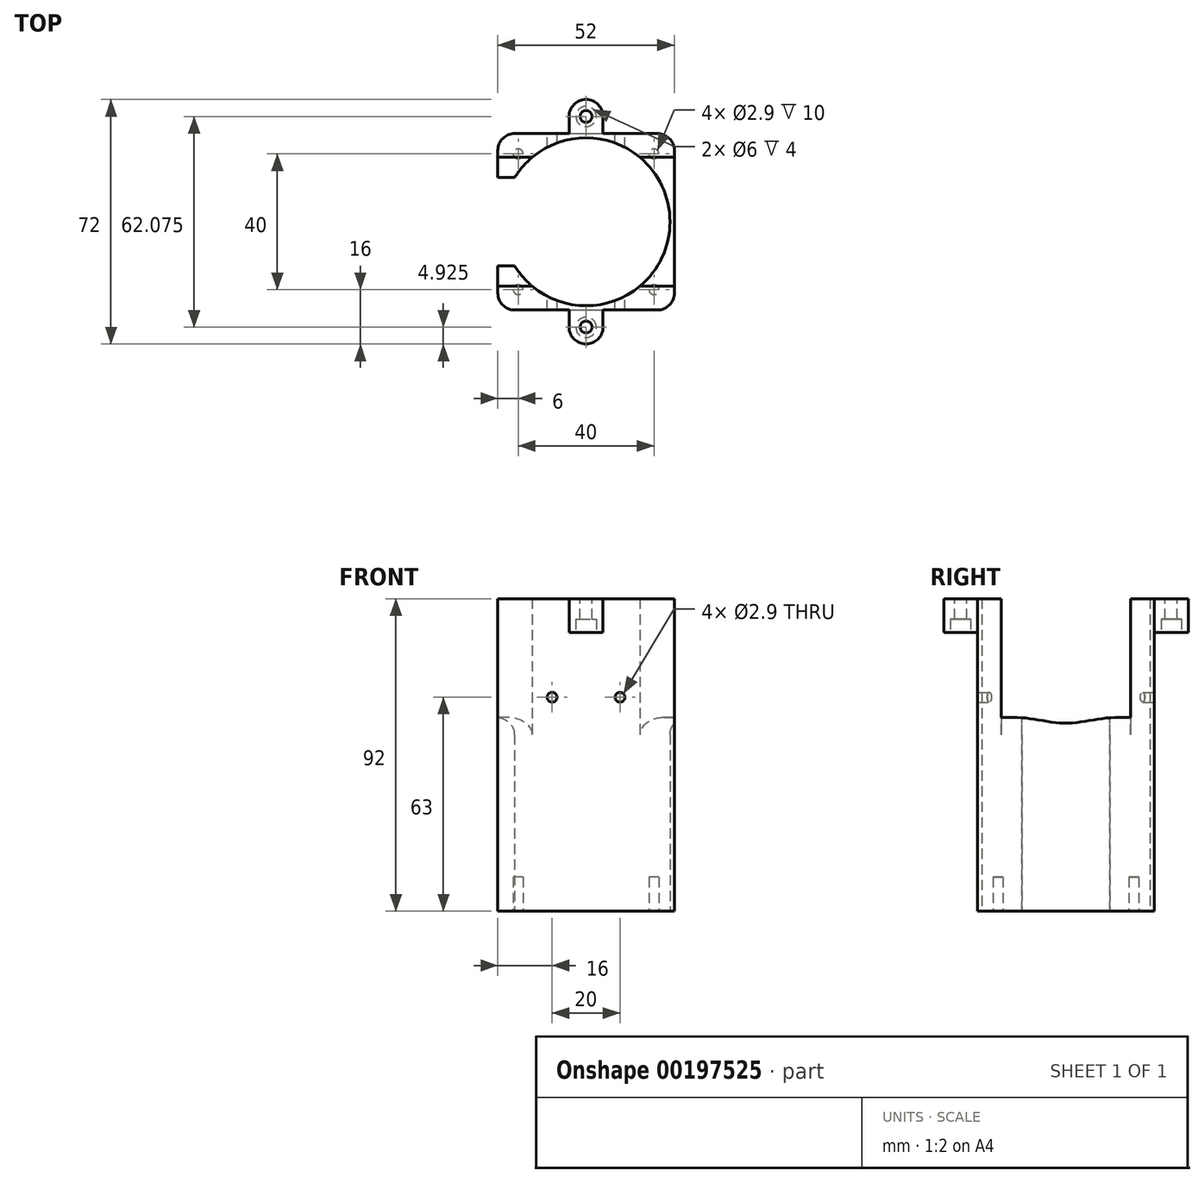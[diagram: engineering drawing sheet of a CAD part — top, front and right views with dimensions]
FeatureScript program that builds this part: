
annotation { "Feature Type Name" : "Feature", "Feature Type Description" : "" }
export const myFeature = defineFeature(function(context is Context, id is Id, definition is map)
    precondition{}
    {
        {
            var Q0;
            Q0=qCreatedBy(makeId("Top.planeOp"),FACE);
            var sketch = newSketch(context, id + "F0", { "sketchPlane" : qUnion([Q0])});
            skLineSegment(sketch, "E0.bottom", {"start": v(-26, 26) * mm, "end": v(26, 26) * mm});
            skLineSegment(sketch, "E0.top", {"start": v(-26, -26) * mm, "end": v(26, -26) * mm});
            skLineSegment(sketch, "E0.left", {"start": v(-26, 26) * mm, "end": v(-26, -26) * mm});
            skLineSegment(sketch, "E0.right", {"start": v(26, 26) * mm, "end": v(26, -26) * mm});
            skCircle(sketch, "E1", {"center": v(-20, 20) * mm, "radius": 1.45 * mm, "construction": true});
            skCircle(sketch, "E2", {"center": v(20, 20) * mm, "radius": 1.45 * mm, "construction": true});
            skCircle(sketch, "E3", {"center": v(20, -20) * mm, "radius": 1.45 * mm, "construction": true});
            skCircle(sketch, "E4", {"center": v(-20, -20) * mm, "radius": 1.45 * mm, "construction": true});
            skCircle(sketch, "E5", {"center": v(0, 0) * mm, "radius": 24.73 * mm});
            skLineSegment(sketch, "E6.bottom", {"start": v(-16.12, -18.75) * mm, "end": v(16.13, -18.75) * mm, "construction": true});
            skLineSegment(sketch, "E6.top", {"start": v(-16.13, 18.75) * mm, "end": v(16.12, 18.75) * mm, "construction": true});
            skLineSegment(sketch, "E6.left", {"start": v(-16.12, -18.75) * mm, "end": v(-16.13, 18.75) * mm, "construction": true});
            skLineSegment(sketch, "E6.right", {"start": v(16.13, -18.75) * mm, "end": v(16.12, 18.75) * mm, "construction": true});
            skCircle(sketch, "E7", {"center": v(0, 0) * mm, "radius": 6 * mm, "construction": true});
            skLineSegment(sketch, "E8.bottom", {"start": v(-5, -36) * mm, "end": v(5, -36) * mm, "construction": true});
            skLineSegment(sketch, "E8.top", {"start": v(-5, -26) * mm, "end": v(5, -26) * mm, "construction": true});
            skLineSegment(sketch, "E8.left", {"start": v(-5, -36) * mm, "end": v(-5, -26) * mm, "construction": true});
            skLineSegment(sketch, "E8.right", {"start": v(5, -36) * mm, "end": v(5, -26) * mm, "construction": true});
            skLineSegment(sketch, "E9.bottom", {"start": v(-5, 26) * mm, "end": v(5, 26) * mm, "construction": true});
            skLineSegment(sketch, "E9.top", {"start": v(-5, 36) * mm, "end": v(5, 36) * mm, "construction": true});
            skLineSegment(sketch, "E9.left", {"start": v(-5, 26) * mm, "end": v(-5, 36) * mm, "construction": true});
            skLineSegment(sketch, "E9.right", {"start": v(5, 26) * mm, "end": v(5, 36) * mm, "construction": true});
            skCircle(sketch, "E10", {"center": v(0, -31) * mm, "radius": 1.75 * mm, "construction": true});
            skPoint(sketch, "E10.centerSnap0", {"position": v(5, -31) * mm});
            skCircle(sketch, "E11", {"center": v(0, 31) * mm, "radius": 1.75 * mm, "construction": true});
            skPoint(sketch, "E11.centerSnap0", {"position": v(5, 31) * mm});
            skSolve(sketch);
        }
        {
            var Q0;
            Q0=qSketchRegion(id+"F0",true);
            extrude(context, id + "F1", {"entities" : qUnion([Q0]), "depth" : 92 * mm});
        }
        {
            var Q0;
            Q0=makeQuery(id+"F1.opExtrude","SWEPT_FACE",FACE,{"disambiguationData":[OSD([sQuery(id+"F0.wireOp",EDGE,"E0.left")])]});
            var sketch = newSketch(context, id + "F2", { "sketchPlane" : qUnion([Q0])});
            skLineSegment(sketch, "E12.top", {"start": v(-19, 92) * mm, "end": v(19, 92) * mm});
            skLineSegment(sketch, "E12.right", {"start": v(19, 57) * mm, "end": v(19, 92) * mm});
            skLineSegment(sketch, "E13", {"start": v(-19, 57) * mm, "end": v(19, 57) * mm});
            skLineSegment(sketch, "E14", {"start": v(-19, 57) * mm, "end": v(-19, 92) * mm});
            skSolve(sketch);
        }
        {
            var Q0;
            Q0=qSketchRegion(id+"F2",true);
            extrude(context, id + "F3", {"entities" : qUnion([Q0]), "operationType" : NewBodyOperationType.REMOVE, "endBound" : BoundingType.THROUGH_ALL, "oppositeDirection" : true, "depth" : 25 * mm});
        }
        {
            var Q0;
            Q0=makeQuery(id+"F1.opExtrude","SWEPT_EDGE",EDGE,{"disambiguationData":[OSD([sQuery(id+"F0.wireOp",EDGE,"E0.bottom"),sQuery(id+"F0.wireOp",EDGE,"E0.left")])]});
            var Q1;
            Q1=makeQuery(id+"F1.opExtrude","SWEPT_EDGE",EDGE,{"disambiguationData":[OSD([sQuery(id+"F0.wireOp",EDGE,"E0.top"),sQuery(id+"F0.wireOp",EDGE,"E0.left")])]});
            var Q2;
            Q2=makeQuery(id+"F1.opExtrude","SWEPT_EDGE",EDGE,{"disambiguationData":[OSD([sQuery(id+"F0.wireOp",EDGE,"E0.bottom"),sQuery(id+"F0.wireOp",EDGE,"E0.right")])]});
            var Q3;
            Q3=makeQuery(id+"F1.opExtrude","SWEPT_EDGE",EDGE,{"disambiguationData":[OSD([sQuery(id+"F0.wireOp",EDGE,"E0.top"),sQuery(id+"F0.wireOp",EDGE,"E0.right")])]});
            fillet(context, id + "F4", {"entities" : qUnion([Q0, Q1, Q2, Q3]), "radius" : 5 * mm, "tangentPropagation" : true, "allowEdgeOverflow" : false});
        }
        {
            var Q0;
            Q0=makeQuery(id+"F3.boolean.opBoolean","INTERSECT",EDGE,{"disambiguationData":[OD(0.0)],"derivedFrom":[makeQuery(id+"F1.opExtrude","SWEPT_FACE",FACE,{"disambiguationData":[OSD([sQuery(id+"F0.wireOp",EDGE,"E5")])]}),makeQuery(id+"F3.opExtrude","SWEPT_FACE",FACE,{"disambiguationData":[OSD([sQuery(id+"F2.wireOp",EDGE,"E13")])]})]});
            var Q1;
            Q1=makeQuery(id+"F3.boolean.opBoolean","INTERSECT",EDGE,{"disambiguationData":[OD(1.0)],"derivedFrom":[makeQuery(id+"F1.opExtrude","SWEPT_FACE",FACE,{"disambiguationData":[OSD([sQuery(id+"F0.wireOp",EDGE,"E5")])]}),makeQuery(id+"F3.opExtrude","SWEPT_FACE",FACE,{"disambiguationData":[OSD([sQuery(id+"F2.wireOp",EDGE,"E13")])]})]});
            fillet(context, id + "F5", {"entities" : qUnion([Q0, Q1]), "radius" : 5 * mm, "tangentPropagation" : true, "allowEdgeOverflow" : false});
        }
        {
            var Q0;
            Q0=makeQuery(id+"F0.imprint","IMPRINT",FACE,{"disambiguationData":[TD([[makeQuery(id+"F0.imprint","IMPRINT",EDGE,{"derivedFrom":sQuery(id+"F0.wireOp",EDGE,"E0.bottom")}),-1.0]])]});
            var sketch = newSketch(context, id + "F6", { "sketchPlane" : qUnion([Q0])});
            skCircle(sketch, "E15.0", {"center": v(-20, -20) * mm, "radius": 1.45 * mm});
            skCircle(sketch, "E16.0", {"center": v(20, -20) * mm, "radius": 1.45 * mm});
            skCircle(sketch, "E17.0", {"center": v(20, 20) * mm, "radius": 1.45 * mm});
            skCircle(sketch, "E18.0", {"center": v(-20, 20) * mm, "radius": 1.45 * mm});
            skSolve(sketch);
        }
        {
            var Q0;
            Q0=qSketchRegion(id+"F6",true);
            var Q1;
            Q1=qConstructionFilter(qBodyType(qCreatedBy(id+"F6",EDGE),BodyType.WIRE),ConstructionObject.NO);
            extrude(context, id + "F7", {"entities" : qUnion([Q0]), "operationType" : NewBodyOperationType.REMOVE, "surfaceEntities" : qUnion([Q1]), "depth" : 10 * mm});
        }
        {
            var Q0;
            Q0=makeQuery(id+"F1.opExtrude","SWEPT_FACE",FACE,{"disambiguationData":[OSD([sQuery(id+"F0.wireOp",EDGE,"E0.bottom")])]});
            var sketch = newSketch(context, id + "F8", { "sketchPlane" : qUnion([Q0])});
            skCircle(sketch, "E19", {"center": v(-10, 63) * mm, "radius": 1.45 * mm});
            skCircle(sketch, "E20", {"center": v(10, 63) * mm, "radius": 1.45 * mm});
            skSolve(sketch);
        }
        {
            var Q0;
            Q0=qSketchRegion(id+"F8",true);
            extrude(context, id + "F9", {"entities" : qUnion([Q0]), "operationType" : NewBodyOperationType.REMOVE, "endBound" : BoundingType.THROUGH_ALL, "oppositeDirection" : true, "depth" : 25 * mm});
        }
        {
            var Q0;
            Q0=makeQuery(id+"F0.imprint","IMPRINT",FACE,{"disambiguationData":[TD([[makeQuery(id+"F0.imprint","IMPRINT",EDGE,{"derivedFrom":sQuery(id+"F0.wireOp",EDGE,"E0.bottom")}),-1.0]])]});
            var sketch = newSketch(context, id + "F10", { "sketchPlane" : qUnion([Q0])});
            skLineSegment(sketch, "E21.bottom", {"start": v(-41.13, -13) * mm, "end": v(-16.13, -13) * mm});
            skLineSegment(sketch, "E21.top", {"start": v(-41.13, 13) * mm, "end": v(-16.13, 13) * mm});
            skLineSegment(sketch, "E21.left", {"start": v(-41.13, -13) * mm, "end": v(-41.13, 13) * mm});
            skLineSegment(sketch, "E21.right", {"start": v(-16.13, -13) * mm, "end": v(-16.13, 13) * mm});
            skSolve(sketch);
        }
        {
            var Q0;
            Q0=qSketchRegion(id+"F10",true);
            extrude(context, id + "F11", {"entities" : qUnion([Q0]), "operationType" : NewBodyOperationType.REMOVE, "endBound" : BoundingType.THROUGH_ALL, "depth" : 25 * mm});
        }
        {
            var Q0;
            {var subQ0=sQuery(id+"F0.wireOp",EDGE,"E5");var subQ1=sQuery(id+"F0.wireOp",EDGE,"E0.right");var subQ2=sQuery(id+"F0.wireOp",EDGE,"E0.left");var subQ3=sQuery(id+"F0.wireOp",EDGE,"E0.bottom");Q0=makeQuery(id+"F3.boolean.opBoolean","SPLIT",FACE,{"disambiguationData":[TD([makeQuery(id+"F1.opExtrude","SWEPT_FACE",FACE,{"disambiguationData":[OSD([subQ3])]})])],"derivedFrom":makeQuery(id+"F1.opExtrude","CAP_FACE",FACE,{"disambiguationData":[OSD([subQ3,sQuery(id+"F0.wireOp",EDGE,"E0.top"),subQ2,subQ1,subQ0])],"isStart":false})});}
            var sketch = newSketch(context, id + "F12", { "sketchPlane" : qUnion([Q0])});
            skLineSegment(sketch, "E22.0", {"start": v(-5, -36) * mm, "end": v(5, -36) * mm});
            skLineSegment(sketch, "E23.0", {"start": v(-5, -36) * mm, "end": v(-5, -26) * mm});
            skLineSegment(sketch, "E24.0", {"start": v(5, -36) * mm, "end": v(5, -26) * mm});
            skCircle(sketch, "E25.0", {"center": v(0, -31) * mm, "radius": 1.75 * mm});
            skLineSegment(sketch, "E26.0", {"start": v(-5, 26) * mm, "end": v(-5, 36) * mm});
            skLineSegment(sketch, "E27.0", {"start": v(-5, 36) * mm, "end": v(5, 36) * mm});
            skLineSegment(sketch, "E28.0", {"start": v(5, 26) * mm, "end": v(5, 36) * mm});
            skCircle(sketch, "E29.0", {"center": v(0, 31) * mm, "radius": 1.75 * mm});
            skLineSegment(sketch, "E30", {"start": v(-5, -26) * mm, "end": v(5, -26) * mm});
            skLineSegment(sketch, "E31", {"start": v(-5, 26) * mm, "end": v(5, 26) * mm});
            skSolve(sketch);
        }
        {
            var Q0;
            Q0=qSketchRegion(id+"F12",true);
            extrude(context, id + "F13", {"entities" : qUnion([Q0]), "operationType" : NewBodyOperationType.ADD, "oppositeDirection" : true, "depth" : 10 * mm});
        }
        {
            var Q0;
            Q0=makeQuery(id+"F13.opExtrude","SWEPT_EDGE",EDGE,{"disambiguationData":[OSD([sQuery(id+"F0.wireOp",EDGE,"E0.top"),sQuery(id+"F12.wireOp",EDGE,"E23.0"),sQuery(id+"F12.wireOp",EDGE,"E30")])]});
            var Q1;
            Q1=makeQuery(id+"F13.opExtrude","SWEPT_EDGE",EDGE,{"disambiguationData":[OSD([sQuery(id+"F0.wireOp",EDGE,"E0.top"),sQuery(id+"F12.wireOp",EDGE,"E24.0"),sQuery(id+"F12.wireOp",EDGE,"E30")])]});
            var Q2;
            Q2=makeQuery(id+"F13.opExtrude","SWEPT_EDGE",EDGE,{"disambiguationData":[OSD([sQuery(id+"F0.wireOp",EDGE,"E0.bottom"),sQuery(id+"F12.wireOp",EDGE,"E26.0"),sQuery(id+"F12.wireOp",EDGE,"E31")])]});
            var Q3;
            Q3=makeQuery(id+"F13.opExtrude","SWEPT_EDGE",EDGE,{"disambiguationData":[OSD([sQuery(id+"F0.wireOp",EDGE,"E0.bottom"),sQuery(id+"F12.wireOp",EDGE,"E28.0"),sQuery(id+"F12.wireOp",EDGE,"E31")])]});
            var Q4;
            Q4=makeQuery(id+"F13.opExtrude","SWEPT_EDGE",EDGE,{"disambiguationData":[OSD([sQuery(id+"F12.wireOp",EDGE,"E27.0"),sQuery(id+"F12.wireOp",EDGE,"E28.0")])]});
            var Q5;
            Q5=makeQuery(id+"F13.opExtrude","SWEPT_EDGE",EDGE,{"disambiguationData":[OSD([sQuery(id+"F12.wireOp",EDGE,"E26.0"),sQuery(id+"F12.wireOp",EDGE,"E27.0")])]});
            var Q6;
            Q6=makeQuery(id+"F13.opExtrude","SWEPT_EDGE",EDGE,{"disambiguationData":[OSD([sQuery(id+"F12.wireOp",EDGE,"E22.0"),sQuery(id+"F12.wireOp",EDGE,"E23.0")])]});
            var Q7;
            Q7=makeQuery(id+"F13.opExtrude","SWEPT_EDGE",EDGE,{"disambiguationData":[OSD([sQuery(id+"F12.wireOp",EDGE,"E22.0"),sQuery(id+"F12.wireOp",EDGE,"E24.0")])]});
            fillet(context, id + "F14", {"entities" : qUnion([Q0, Q1, Q2, Q3, Q4, Q5, Q6, Q7]), "radius" : 5 * mm, "tangentPropagation" : true, "allowEdgeOverflow" : false});
        }
        {
            var Q0;
            Q0=makeQuery(id+"F13.opExtrude","CAP_FACE",FACE,{"disambiguationData":[OSD([sQuery(id+"F12.wireOp",EDGE,"E26.0"),sQuery(id+"F12.wireOp",EDGE,"E27.0"),sQuery(id+"F12.wireOp",EDGE,"E28.0"),sQuery(id+"F12.wireOp",EDGE,"E29.0"),sQuery(id+"F12.wireOp",EDGE,"E31")])],"isStart":false});
            var sketch = newSketch(context, id + "F15", { "sketchPlane" : qUnion([Q0])});
            skCircle(sketch, "E32", {"center": v(0, 31.07) * mm, "radius": 3 * mm});
            skCircle(sketch, "E33", {"center": v(0, -31) * mm, "radius": 3 * mm});
            skSolve(sketch);
        }
        {
            var Q0;
            Q0=qSketchRegion(id+"F15",true);
            extrude(context, id + "F16", {"entities" : qUnion([Q0]), "operationType" : NewBodyOperationType.REMOVE, "oppositeDirection" : true, "depth" : 4 * mm});
        }
    });
